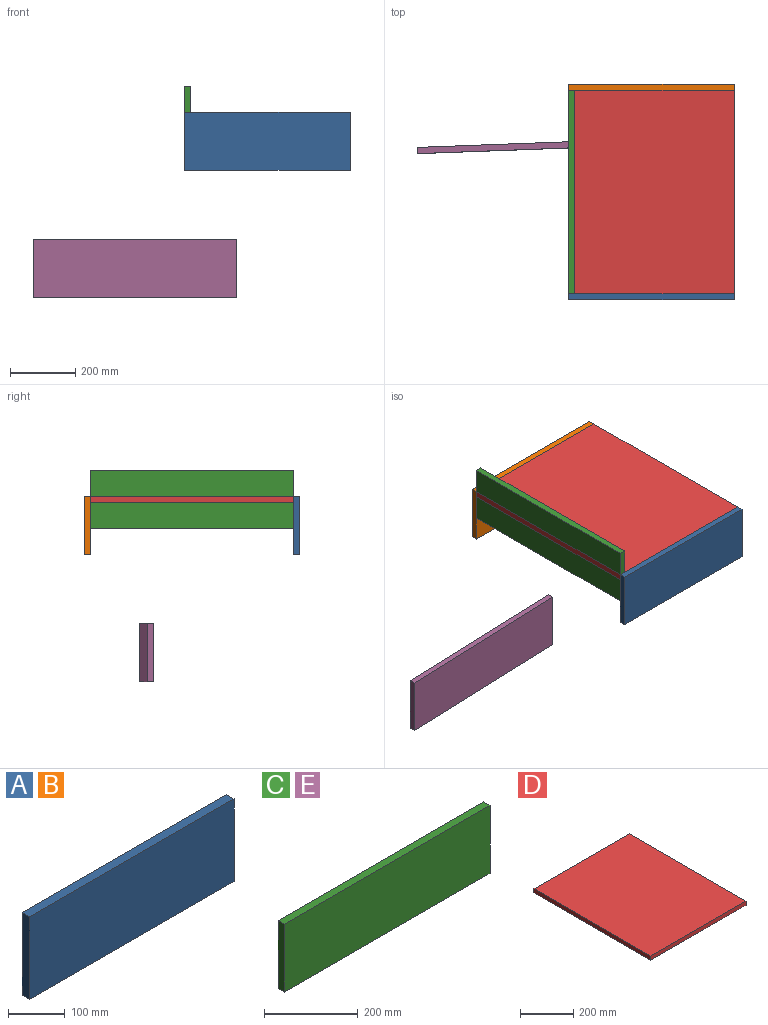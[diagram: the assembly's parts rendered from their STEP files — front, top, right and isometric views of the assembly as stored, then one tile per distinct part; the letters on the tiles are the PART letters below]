
ASSEMBLY  parts=5 mates=5
PART A: 6 faces, bbox 508x19.1x177.8 mm
  f0: plane 508x177.8mm, normal (0,1,0), area 90322.4mm2, adj f1,f3,f4,f5
  f1: plane 177.8x19.05mm, normal (1,0,0), area 3387.1mm2, adj f0,f2,f4,f5
  f2: plane 508x177.8mm, normal (0,-1,0), area 90322.4mm2, adj f1,f3,f4,f5
  f3: plane 177.8x19.05mm, normal (-1,0,0), area 3387.1mm2, adj f0,f2,f4,f5
  f4: plane 508x19.05mm, normal (0,0,-1), area 9677.4mm2, adj f0,f1,f2,f3
  f5: plane 508x19.05mm, normal (0,0,1), area 9677.4mm2, adj f0,f1,f2,f3
PART B: same geometry as A
PART C: 6 faces, bbox 622.3x19.1x177.8 mm
  f0: plane 622.3x177.8mm, normal (0,1,0), area 110644.9mm2, adj f1,f3,f4,f5
  f1: plane 177.8x19.05mm, normal (1,0,0), area 3387.1mm2, adj f0,f2,f3,f4
  f2: plane 622.3x177.8mm, normal (0,-1,0), area 110644.9mm2, adj f1,f3,f4,f5
  f3: plane 622.3x19.05mm, normal (0,0,-1), area 11854.8mm2, adj f0,f1,f2,f5
  f4: plane 622.3x19.05mm, normal (0,0,1), area 11854.8mm2, adj f0,f1,f2,f5
  f5: plane 177.8x19.05mm, normal (-1,0,0), area 3387.1mm2, adj f0,f2,f3,f4
PART D: 6 faces, bbox 508x622.3x19.1 mm
  f0: plane 508x19.05mm, normal (0,-1,0), area 9677.4mm2, adj f1,f3,f4,f5
  f1: plane 622.3x19.05mm, normal (1,0,0), area 11854.8mm2, adj f0,f2,f4,f5
  f2: plane 508x19.05mm, normal (0,1,0), area 9677.4mm2, adj f1,f3,f4,f5
  f3: plane 622.3x19.05mm, normal (-1,0,0), area 11854.8mm2, adj f0,f2,f4,f5
  f4: plane 622.3x508mm, normal (0,0,1), area 316128.4mm2, adj f0,f1,f2,f3
  f5: plane 622.3x508mm, normal (0,0,-1), area 316128.4mm2, adj f0,f1,f2,f3
PART E: same geometry as C
PLACE A rot(axis=(0,0,1),0deg) t=(49.87,-657.15,102.79)mm
PLACE B rot(axis=(0,0,1),0deg) t=(49.87,-15.8,102.79)mm
PLACE C rot(axis=(0,0,-1),90deg) t=(-602.9,-59.75,182.17)mm
PLACE D rot(axis=(0,0,1),0deg) t=(49.87,46.54,83.74)mm
PLACE E rot(axis=(0,0,-1),177.9deg) t=(-300.64,544.81,-287.84)mm
MATE planar B.f2 <-> D.f2  axis (0,-1,0) through (114.26,244.16,13.89)mm
MATE planar A.f0 <-> D.f0  axis (0,1,0) through (114.26,-378.14,102.79)mm
MATE planar C.f2 <-> D.f3  axis (-1,0,0) through (-139.74,-66.99,93.27)mm
MATE planar D.f4 <-> B.f5  axis (0,0,1) through (114.26,244.16,102.79)mm
MATE planar A.f5 <-> D.f4  axis (0,0,1) through (114.26,-387.66,102.79)mm
